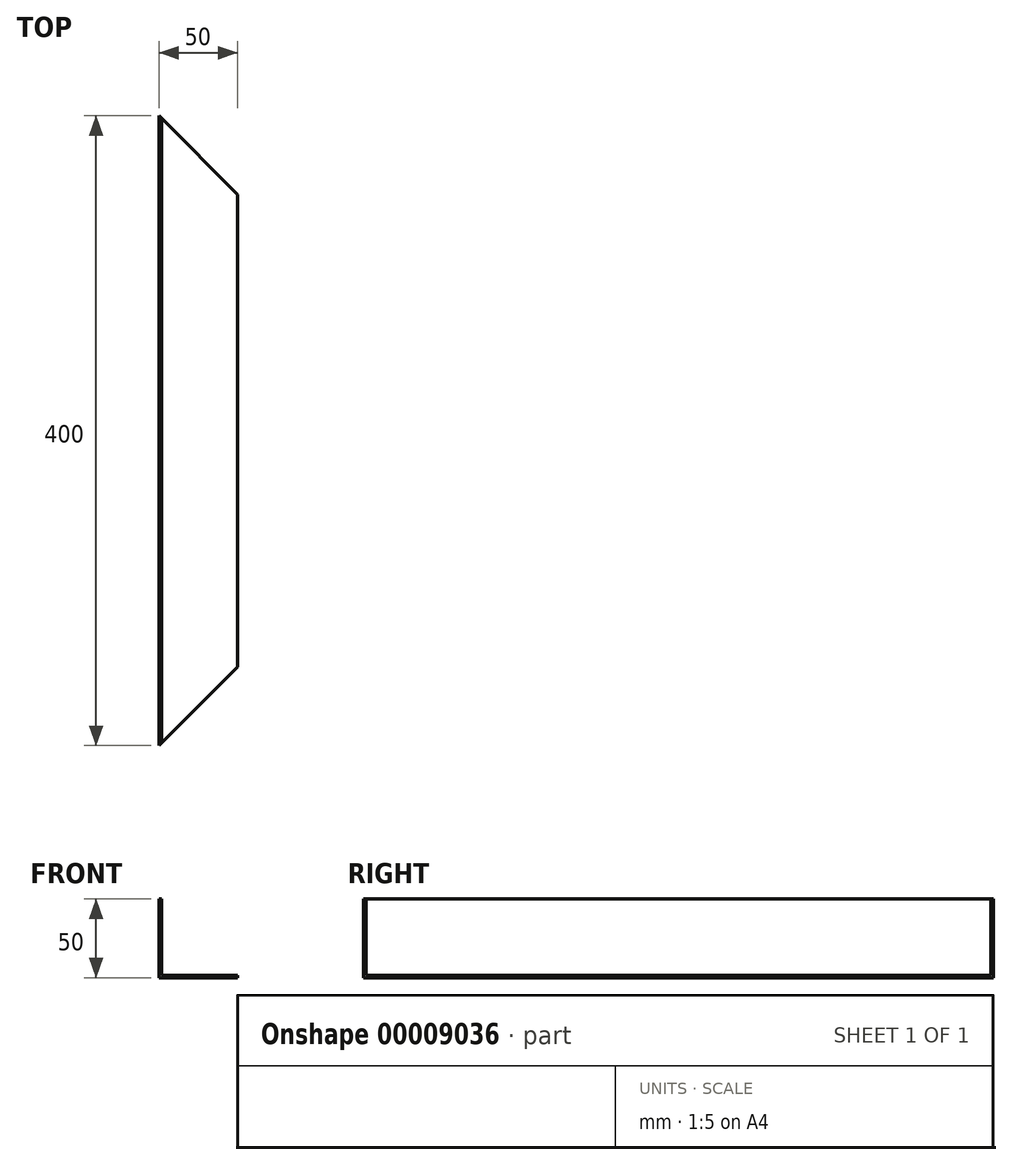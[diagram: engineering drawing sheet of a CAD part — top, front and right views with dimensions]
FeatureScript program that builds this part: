
annotation { "Feature Type Name" : "Feature", "Feature Type Description" : "" }
export const myFeature = defineFeature(function(context is Context, id is Id, definition is map)
    precondition{}
    {
        {
            var Q0;
            Q0=qCreatedBy(makeId("Front.planeOp"),FACE);
            var sketch = newSketch(context, id + "F0", { "sketchPlane" : qUnion([Q0])});
            skLineSegment(sketch, "E0.bottom", {"start": v(-33, 48.4) * mm, "end": v(-31.4, 48.4) * mm});
            skLineSegment(sketch, "E0.top", {"start": v(-33, -1.6) * mm, "end": v(-31.4, -1.6) * mm});
            skLineSegment(sketch, "E0.left", {"start": v(-33, 48.4) * mm, "end": v(-33, -1.6) * mm});
            skLineSegment(sketch, "E0.right", {"start": v(-31.4, 48.4) * mm, "end": v(-31.4, -1.6) * mm});
            skLineSegment(sketch, "E1.bottom", {"start": v(-33, -1.6) * mm, "end": v(17, -1.6) * mm});
            skLineSegment(sketch, "E1.top", {"start": v(-33, 0) * mm, "end": v(17, 0) * mm});
            skLineSegment(sketch, "E1.left", {"start": v(-33, -1.6) * mm, "end": v(-33, 0) * mm});
            skLineSegment(sketch, "E1.right", {"start": v(17, -1.6) * mm, "end": v(17, 0) * mm});
            skSolve(sketch);
        }
        {
            var Q0;
            Q0 = qSketchRegion(id + "F0", true);
            extrude(context, id + "F1", {"entities" : qUnion([Q0]), "depth" : 400 * mm});
        }
        {
            var Q0;
            Q0=makeQuery(id+"F1.opExtrude","SWEPT_FACE",FACE,{"disambiguationData":[OSD([sQuery(id+"F0.wireOp",EDGE,"E1.bottom")])]});
            var sketch = newSketch(context, id + "F2", { "sketchPlane" : qUnion([Q0])});
            skLineSegment(sketch, "E2", {"start": v(-33, 0) * mm, "end": v(17, 50) * mm});
            skLineSegment(sketch, "E3", {"start": v(17, 50) * mm, "end": v(17, 0) * mm});
            skLineSegment(sketch, "E4", {"start": v(17, 0) * mm, "end": v(-33, 0) * mm});
            skSolve(sketch);
        }
        {
            var Q0;
            Q0 = qSketchRegion(id + "F2", true);
            extrude(context, id + "F3", {"entities" : qUnion([Q0]), "operationType" : NewBodyOperationType.REMOVE, "endBound" : BoundingType.THROUGH_ALL, "oppositeDirection" : true, "depth" : 25 * mm});
        }
        {
            var Q0;
            Q0=makeQuery(id+"F1.opExtrude","SWEPT_FACE",FACE,{"disambiguationData":[OSD([sQuery(id+"F0.wireOp",EDGE,"E1.bottom")])]});
            var sketch = newSketch(context, id + "F4", { "sketchPlane" : qUnion([Q0])});
            skLineSegment(sketch, "E5", {"start": v(-33, 400) * mm, "end": v(17, 350) * mm});
            skLineSegment(sketch, "E6", {"start": v(17, 350) * mm, "end": v(17, 400) * mm});
            skLineSegment(sketch, "E7", {"start": v(17, 400) * mm, "end": v(-33, 400) * mm});
            skSolve(sketch);
        }
        {
            var Q0;
            Q0 = qSketchRegion(id + "F4", true);
            extrude(context, id + "F5", {"entities" : qUnion([Q0]), "operationType" : NewBodyOperationType.REMOVE, "endBound" : BoundingType.THROUGH_ALL, "oppositeDirection" : true, "depth" : 25 * mm});
        }
    });
